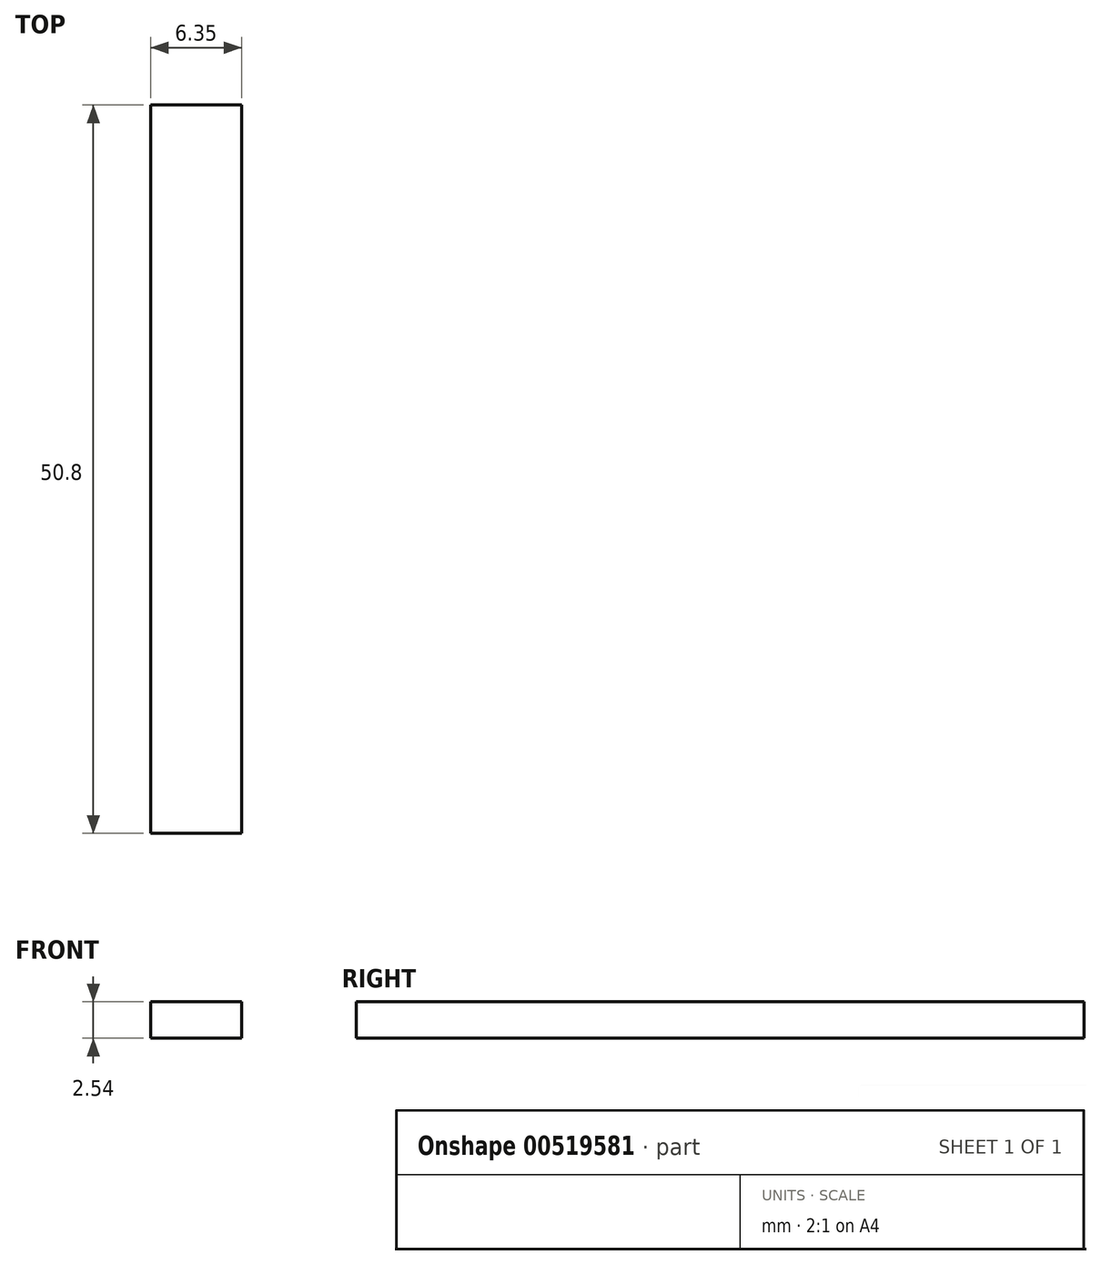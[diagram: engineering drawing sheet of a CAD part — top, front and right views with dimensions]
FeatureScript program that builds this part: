
annotation { "Feature Type Name" : "Feature", "Feature Type Description" : "" }
export const myFeature = defineFeature(function(context is Context, id is Id, definition is map)
    precondition{}
    {
        {
            var Q0;
            Q0=qCreatedBy(makeId("Top.planeOp"),FACE);
            var sketch = newSketch(context, id + "F0", { "sketchPlane" : qUnion([Q0])});
            skLineSegment(sketch, "E0.bottom", {"start": v(-47.64, 34.27) * mm, "end": v(-41.29, 34.27) * mm});
            skLineSegment(sketch, "E0.top", {"start": v(-47.64, -16.53) * mm, "end": v(-41.29, -16.53) * mm});
            skLineSegment(sketch, "E0.left", {"start": v(-47.64, 34.27) * mm, "end": v(-47.64, -16.53) * mm});
            skLineSegment(sketch, "E0.right", {"start": v(-41.29, 34.27) * mm, "end": v(-41.29, -16.53) * mm});
            skSolve(sketch);
        }
        {
            var Q0;
            Q0 = qSketchRegion(id + "F0", true);
            extrude(context, id + "F1", {"entities" : qUnion([Q0]), "depth" : 2.54 * mm, "offsetDistance" : 25.4 * mm});
        }
    });
